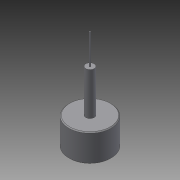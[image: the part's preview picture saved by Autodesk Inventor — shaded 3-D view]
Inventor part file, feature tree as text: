
AUTODESK INVENTOR PART (.ipt)
format: ipt  version: 2015 (Build 190159000, 159)  size: 97,792 bytes
history: native  units: in
note: dims shown in document units (in); Inventor stores cm internally (conversion verified against a paired STEP export)
features: revolve x1, chamfer x1
ambient origin geometry x8: Origin, YZ Plane, XZ Plane, XY Plane, X Axis, Y Axis, Z Axis, Center Point
bodies: Solid1 (feature_tree)
feature tree (2):
  revolve  "Revolution1"  [1 undecoded]
  chamfer  "Chamfer1"  Distance=2.5in
note: 1 required parameter value undecoded (feature->parameter linkage not recoverable at this tier; creation-order binding heuristic only, values carry confidence <= 0.55)
